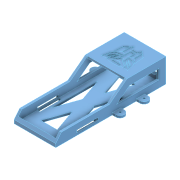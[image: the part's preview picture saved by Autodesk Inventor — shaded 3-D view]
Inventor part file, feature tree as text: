
AUTODESK INVENTOR PART (.ipt)
format: ipt  version: 2022 (Build 260153000, 153)  size: 469,504 bytes
history: native  units: mm
features: sketch x13, extrude x11, projected_geometry x10, fillet x2, rib x1, mirror x1, chamfer x1, hole x1
ambient origin geometry x8: Origin, YZ Plane, XZ Plane, XY Plane, X Axis, Y Axis, Z Axis, Center Point
bodies: Body1 (feature_tree)
feature tree (40):
  extrude  "Extrusion3"  Depth=143.0mm
  extrude  "Extrusion4"  Depth=3.0mm TaperAngle=0.0deg
  extrude  "Extrusion5"  Depth=3.0mm
  extrude  "Extrusion6"  Depth=5.0mm
  extrude  "Velcro Strap Hole"  Depth=5.0mm TaperAngle=0.0deg
  rib  "Rib1"
  mirror  "Mirror2"
  extrude  "Extrusion13"  Depth=5.0mm
  chamfer  "Chamfer4"  Distance=10.0mm
  extrude  "Extrusion8"  Depth=1.0mm
  extrude  "Extrusion9"  Depth=8.0mm TaperAngle=45.0deg
  hole  "Mounting Holes"  [1 undecoded]
  fillet  "Fillet1"  Radius=6.0mm
  extrude  "Extrusion10"  Depth=5.0mm
  extrude  "Autobots Logo"  Depth=30.0mm
  extrude  "Velcro Strap Hole 2"  Depth=34.0mm
  fillet  "Fillet2"  Radius=5.0mm
  sketch  "Sketch4"  dims[d25=51.0mm d26=143.0mm]
  sketch  "Sketch5"  dims[d27=4.0mm d28=3.0mm d29=0.0mm]
  sketch  "Sketch6"  dims[d30=3.0mm d31=3.0mm]
  sketch  "Sketch7"  dims[d33=50.0mm d34=0.0mm d36=5.0mm]
  sketch  "Sketch8"  dims[d37=3.0mm d38=5.0mm d39=0.0mm]
  sketch  "Sketch9"  dims[d40=15.0mm d41=5.0mm]
  sketch  "Sketch10"  dims[d42=0.0mm]
  sketch  "Sketch11"  dims[d43=30.0mm]
  sketch  "Sketch12"  dims[d45=4.0mm]
  sketch  "Sketch13"  dims[d46=45.0mm d47=10.0mm d48=0.0mm]
  sketch  "Sketch14"  dims[d49=25.0mm d50=1.0mm]
  sketch  "Sketch15"  dims[d51=3.0mm d52=0.0mm d53=0.0mm d54=1.0mm d55=1.0mm d56=8.0mm d57=10.0mm d58=45.0deg]
  sketch  "Sketch16"  dims[d59=10.0mm d60=10.0mm d61=0.0mm d62=6.0mm d64=5.0mm d65=30.0mm d66=34.0mm d67=5.0mm d68=6.0mm d69=10.0mm d70=0.0mm d71=3.4mm d72=6.0mm d73=4.0mm d74=2.0mm d75=90.0deg d76=6.0mm d77=0.0mm d78=5.0mm d81=20.0mm d82=10.0mm d83=15.0mm d84=10.0mm d85=0.0mm d86=1.0mm d87=0.0mm d88=28.0mm d89=3.0mm d90=3.0mm d91=10.0mm d92=0.0mm d93=3.0mm d94=3.0mm d95=10.0mm d96=0.0mm d97=1.0mm]
  projected_geometry  "Project Cut Edges2"
  projected_geometry  "Project Cut Edges3"
  projected_geometry  "Project Cut Edges4"
  projected_geometry  "Project Cut Edges5"
  projected_geometry  "Project Cut Edges6"
  projected_geometry  "Project Cut Edges7"
  projected_geometry  "Project Cut Edges8"
  projected_geometry  "Project Cut Edges9"
  projected_geometry  "Project Cut Edges10"
  projected_geometry  "Project Cut Edges11"
note: 1 required parameter value undecoded (feature->parameter linkage not recoverable at this tier; creation-order binding heuristic only, values carry confidence <= 0.55)
